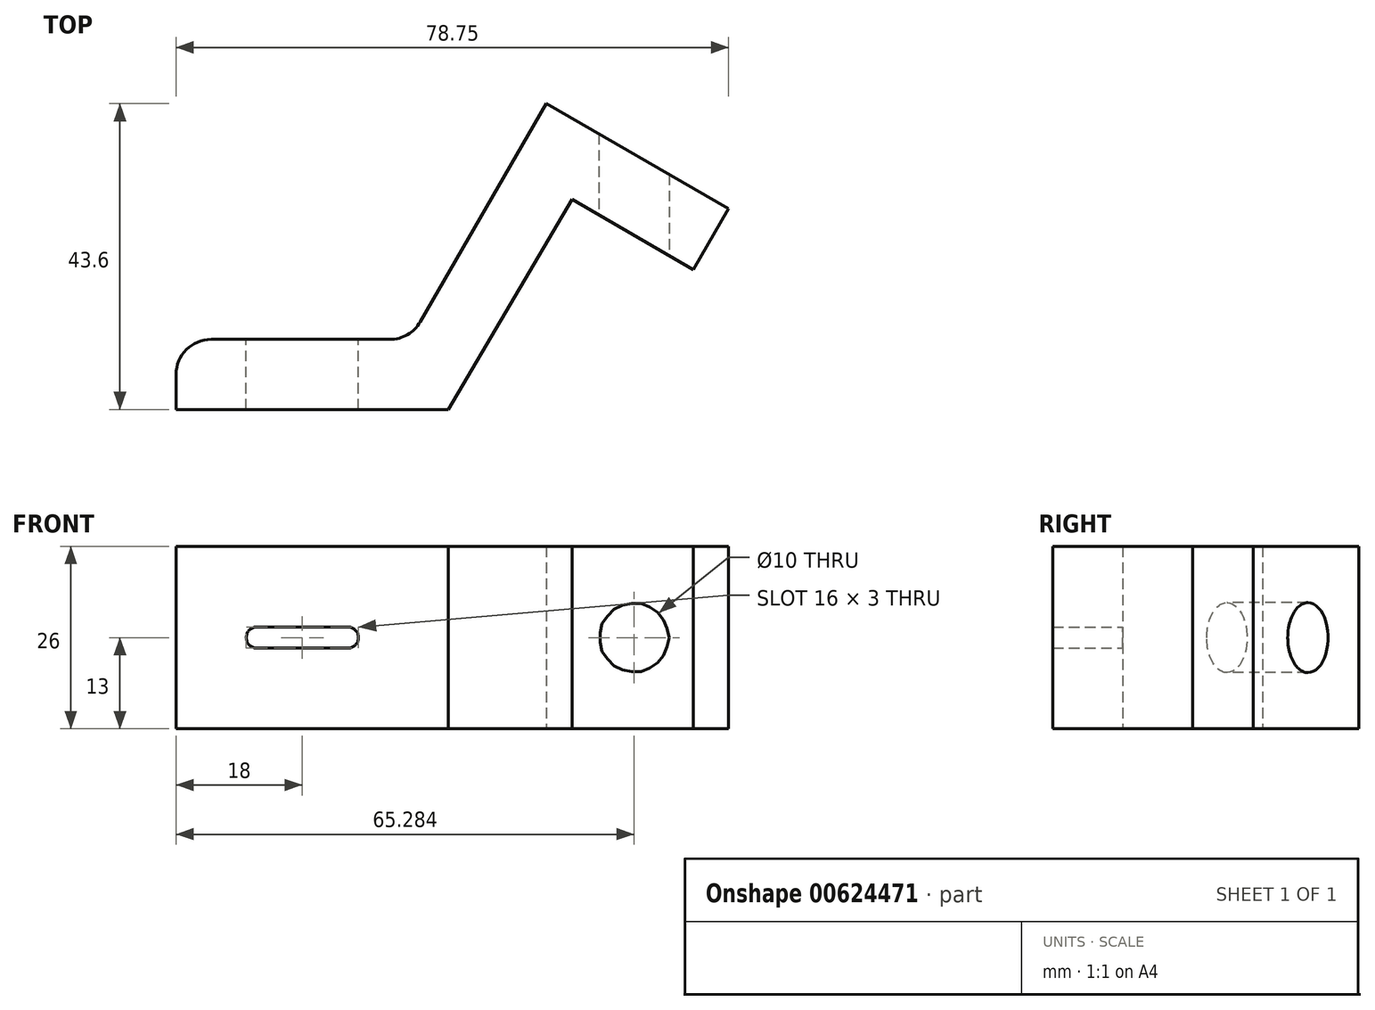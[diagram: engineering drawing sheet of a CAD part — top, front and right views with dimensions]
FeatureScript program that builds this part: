
annotation { "Feature Type Name" : "Feature", "Feature Type Description" : "" }
export const myFeature = defineFeature(function(context is Context, id is Id, definition is map)
    precondition{}
    {
        {
            var Q0;
            Q0=qCreatedBy(makeId("Top.planeOp"),FACE);
            var sketch = newSketch(context, id + "F0", { "sketchPlane" : qUnion([Q0])});
            skLineSegment(sketch, "E0", {"start": v(-38.8, 0) * mm, "end": v(0, 0) * mm});
            skLineSegment(sketch, "E1", {"start": v(-38.8, 0) * mm, "end": v(-38.8, 5) * mm});
            skLineSegment(sketch, "E2", {"start": v(-33.8, 10) * mm, "end": v(-8.31, 10) * mm});
            skLineSegment(sketch, "E3", {"start": v(-3.98, 12.5) * mm, "end": v(13.97, 43.6) * mm});
            skLineSegment(sketch, "E4", {"start": v(13.97, 43.6) * mm, "end": v(39.95, 28.6) * mm});
            skLineSegment(sketch, "E5", {"start": v(39.95, 28.6) * mm, "end": v(34.95, 19.94) * mm});
            skLineSegment(sketch, "E6", {"start": v(34.95, 19.94) * mm, "end": v(17.63, 29.94) * mm});
            skLineSegment(sketch, "E7", {"start": v(17.63, 29.94) * mm, "end": v(0, 0) * mm});
            skPoint(sketch, "E8.visualSharp", {"position": v(-38.8, 10) * mm});
            skArc(sketch, "E8.filletArc", {"start": v(-33.8, 10) * mm, "mid": v(-37.34, 8.54) * mm, "end": v(-38.8, 5) * mm});
            skPoint(sketch, "E9.visualSharp", {"position": v(-5.43, 10) * mm});
            skArc(sketch, "E9.filletArc", {"start": v(-8.31, 10) * mm, "mid": v(-5.81, 10.67) * mm, "end": v(-3.98, 12.5) * mm});
            skSolve(sketch);
        }
        {
            var Q0;
            Q0=makeQuery(id+"F0.imprint","IMPRINT",FACE,{"disambiguationData":[TD([[makeQuery(id+"F0.imprint","IMPRINT",EDGE,{"derivedFrom":sQuery(id+"F0.wireOp",EDGE,"E0")}),1.0]])]});
            extrude(context, id + "F1", {"entities" : qUnion([Q0]), "depth" : 26 * mm, "offsetDistance" : 25 * mm});
        }
        {
            var Q0;
            Q0=makeQuery(id+"F1.opExtrude","SWEPT_FACE",FACE,{"disambiguationData":[OSD([sQuery(id+"F0.wireOp",EDGE,"E2")])]});
            var sketch = newSketch(context, id + "F2", { "sketchPlane" : qUnion([Q0])});
            skCircle(sketch, "E10", {"center": v(27.3, 13) * mm, "radius": 1.5 * mm});
            skPoint(sketch, "E10.centerSnap0", {"position": v(33.8, 13) * mm});
            skCircle(sketch, "E11", {"center": v(14.3, 13) * mm, "radius": 1.5 * mm});
            skLineSegment(sketch, "E12", {"start": v(14.3, 11.5) * mm, "end": v(27.3, 11.5) * mm});
            skLineSegment(sketch, "E13", {"start": v(14.3, 14.5) * mm, "end": v(27.3, 14.5) * mm});
            skSolve(sketch);
        }
        {
            var Q0;
            {var subQ0=sQuery(id+"F2.wireOp",EDGE,"E10");var subQ1=makeQuery(id+"F2.imprint","INTERSECT",VERTEX,{"derivedFrom":[subQ0,sQuery(id+"F2.wireOp",EDGE,"E12")]});Q0=makeQuery(id+"F2.imprint","IMPRINT",FACE,{"disambiguationData":[TD([[makeQuery(id+"F2.imprint","IMPRINT",EDGE,{"disambiguationData":[TD([[subQ1,1.0]])],"derivedFrom":subQ0}),1.0]])]});}
            var Q1;
            {var subQ0=sQuery(id+"F2.wireOp",EDGE,"E11");var subQ1=makeQuery(id+"F2.imprint","INTERSECT",VERTEX,{"derivedFrom":[subQ0,sQuery(id+"F2.wireOp",EDGE,"E12")]});Q1=makeQuery(id+"F2.imprint","IMPRINT",FACE,{"disambiguationData":[TD([[makeQuery(id+"F2.imprint","IMPRINT",EDGE,{"disambiguationData":[TD([[subQ1,1.0]])],"derivedFrom":subQ0}),1.0]])]});}
            var Q2;
            {var subQ0=sQuery(id+"F2.wireOp",EDGE,"E12");Q2=makeQuery(id+"F2.imprint","IMPRINT",FACE,{"disambiguationData":[TD([[makeQuery(id+"F2.imprint","IMPRINT",EDGE,{"derivedFrom":subQ0}),1.0]])]});}
            extrude(context, id + "F3", {"entities" : qUnion([Q0, Q1, Q2]), "operationType" : NewBodyOperationType.REMOVE, "oppositeDirection" : true, "depth" : 25 * mm, "offsetDistance" : 25 * mm});
        }
        {
            var Q0;
            Q0=qCreatedBy(makeId("Front.planeOp"),FACE);
            var sketch = newSketch(context, id + "F4", { "sketchPlane" : qUnion([Q0])});
            skCircle(sketch, "E14", {"center": v(26.48, 13) * mm, "radius": 7 * mm});
            skSolve(sketch);
        }
        {
            var Q0;
            Q0=sQuery(id+"F4.wireOp",VERTEX,"E14.center");
            var Q1;
            Q1=makeQuery(id+"F1.opExtrude","SWEPT_BODY",BODY,{"disambiguationData":[OSD([sQuery(id+"F0.wireOp",EDGE,"E0"),sQuery(id+"F0.wireOp",EDGE,"E1"),sQuery(id+"F0.wireOp",EDGE,"E2"),sQuery(id+"F0.wireOp",EDGE,"E3"),sQuery(id+"F0.wireOp",EDGE,"E4"),sQuery(id+"F0.wireOp",EDGE,"E5"),sQuery(id+"F0.wireOp",EDGE,"E6"),sQuery(id+"F0.wireOp",EDGE,"E7"),sQuery(id+"F0.wireOp",EDGE,"E8.filletArc"),sQuery(id+"F0.wireOp",EDGE,"E9.filletArc")])]});
            hole(context, id + "F5", {"style" : HoleStyle.SIMPLE, "endStyle" : HoleEndStyle.THROUGH, "holeDiameter" : 10 * mm, "majorDiameter" : 5 * mm, "isTappedThrough" : true, "tappedDepth" : 12 * mm, "tapClearance" : 3, "locations" : qUnion([Q0]), "scope" : qUnion([Q1])});
        }
    });
